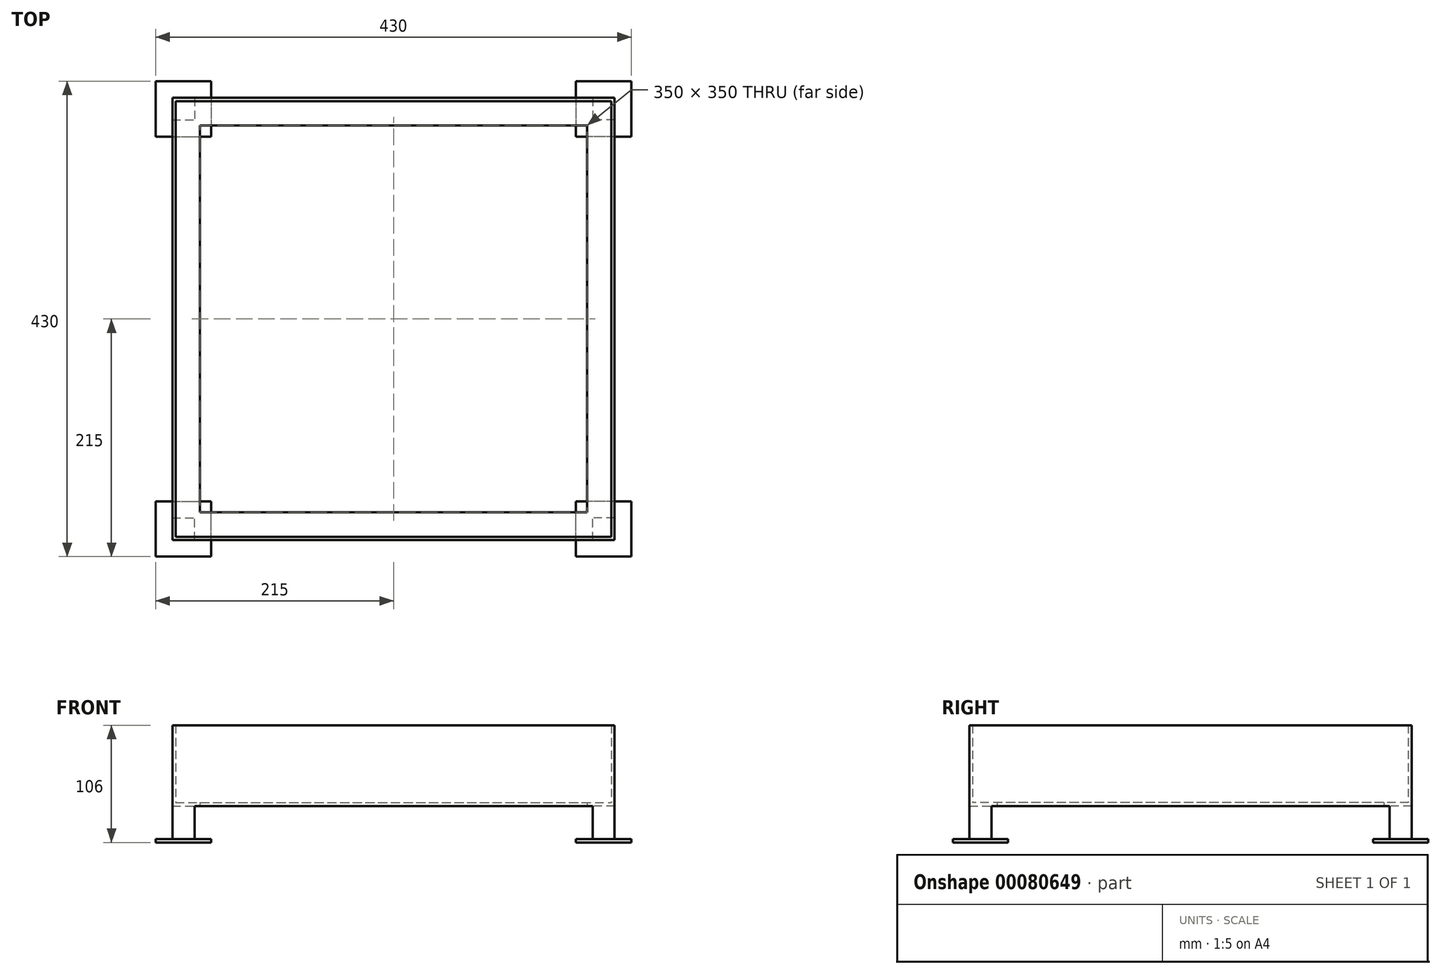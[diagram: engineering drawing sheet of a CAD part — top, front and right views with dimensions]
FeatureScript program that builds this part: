
annotation { "Feature Type Name" : "Feature", "Feature Type Description" : "" }
export const myFeature = defineFeature(function(context is Context, id is Id, definition is map)
    precondition{}
    {
        {
            var Q0;
            Q0=qCreatedBy(makeId("Top.planeOp"),FACE);
            var sketch = newSketch(context, id + "F0", { "sketchPlane" : qUnion([Q0])});
            skLineSegment(sketch, "E0.bottom", {"start": v(-200, 200) * mm, "end": v(200, 200) * mm});
            skLineSegment(sketch, "E0.top", {"start": v(-200, -200) * mm, "end": v(200, -200) * mm});
            skLineSegment(sketch, "E0.left", {"start": v(-200, 200) * mm, "end": v(-200, -200) * mm});
            skLineSegment(sketch, "E0.right", {"start": v(200, 200) * mm, "end": v(200, -200) * mm});
            skPoint(sketch, "E0.middle", {"position": v(0, 0) * mm});
            skLineSegment(sketch, "E1.bottom", {"start": v(-175, 175) * mm, "end": v(175, 175) * mm});
            skLineSegment(sketch, "E1.top", {"start": v(-175, -175) * mm, "end": v(175, -175) * mm});
            skLineSegment(sketch, "E1.left", {"start": v(-175, 175) * mm, "end": v(-175, -175) * mm});
            skLineSegment(sketch, "E1.right", {"start": v(175, 175) * mm, "end": v(175, -175) * mm});
            skSolve(sketch);
        }
        {
            var Q0;
            Q0=makeQuery(id+"F0.imprint","IMPRINT",FACE,{"disambiguationData":[TD([[makeQuery(id+"F0.imprint","IMPRINT",EDGE,{"derivedFrom":sQuery(id+"F0.wireOp",EDGE,"E0.bottom")}),-1.0]])]});
            extrude(context, id + "F1", {"entities" : qUnion([Q0]), "depth" : 3 * mm});
        }
        {
            var Q0;
            Q0=makeQuery(id+"F1.opExtrude","CAP_FACE",FACE,{"disambiguationData":[OSD([sQuery(id+"F0.wireOp",EDGE,"E0.bottom"),sQuery(id+"F0.wireOp",EDGE,"E0.top"),sQuery(id+"F0.wireOp",EDGE,"E0.left"),sQuery(id+"F0.wireOp",EDGE,"E0.right"),sQuery(id+"F0.wireOp",EDGE,"E1.bottom"),sQuery(id+"F0.wireOp",EDGE,"E1.top"),sQuery(id+"F0.wireOp",EDGE,"E1.left"),sQuery(id+"F0.wireOp",EDGE,"E1.right")])],"isStart":false});
            var sketch = newSketch(context, id + "F2", { "sketchPlane" : qUnion([Q0])});
            skLineSegment(sketch, "E2.0", {"start": v(-200, 200) * mm, "end": v(-200, -200) * mm});
            skLineSegment(sketch, "E3.0", {"start": v(-200, 200) * mm, "end": v(200, 200) * mm});
            skLineSegment(sketch, "E4.0", {"start": v(200, 200) * mm, "end": v(200, -200) * mm});
            skLineSegment(sketch, "E5.0", {"start": v(-200, -200) * mm, "end": v(200, -200) * mm});
            skLineSegment(sketch, "E6.bottom", {"start": v(-197, 197) * mm, "end": v(197, 197) * mm});
            skLineSegment(sketch, "E6.top", {"start": v(-197, -197) * mm, "end": v(197, -197) * mm});
            skLineSegment(sketch, "E6.left", {"start": v(-197, 197) * mm, "end": v(-197, -197) * mm});
            skLineSegment(sketch, "E6.right", {"start": v(197, 197) * mm, "end": v(197, -197) * mm});
            skPoint(sketch, "E6.middle", {"position": v(0, 0) * mm});
            skSolve(sketch);
        }
        {
            var Q0;
            Q0=makeQuery(id+"F2.imprint","IMPRINT",FACE,{"disambiguationData":[TD([[makeQuery(id+"F2.imprint","IMPRINT",EDGE,{"derivedFrom":sQuery(id+"F2.wireOp",EDGE,"E2.0")}),1.0]])]});
            extrude(context, id + "F3", {"entities" : qUnion([Q0]), "operationType" : NewBodyOperationType.ADD, "depth" : 70 * mm});
        }
        {
            var Q0;
            Q0=makeQuery(id+"F1.opExtrude","CAP_FACE",FACE,{"disambiguationData":[OSD([sQuery(id+"F0.wireOp",EDGE,"E0.bottom"),sQuery(id+"F0.wireOp",EDGE,"E0.top"),sQuery(id+"F0.wireOp",EDGE,"E0.left"),sQuery(id+"F0.wireOp",EDGE,"E0.right"),sQuery(id+"F0.wireOp",EDGE,"E1.bottom"),sQuery(id+"F0.wireOp",EDGE,"E1.top"),sQuery(id+"F0.wireOp",EDGE,"E1.left"),sQuery(id+"F0.wireOp",EDGE,"E1.right")])],"isStart":true});
            var sketch = newSketch(context, id + "F4", { "sketchPlane" : qUnion([Q0])});
            skLineSegment(sketch, "E7.bottom", {"start": v(-200, 200) * mm, "end": v(-180, 200) * mm});
            skLineSegment(sketch, "E7.top", {"start": v(-200, 180) * mm, "end": v(-180, 180) * mm});
            skLineSegment(sketch, "E7.left", {"start": v(-200, 200) * mm, "end": v(-200, 180) * mm});
            skLineSegment(sketch, "E7.right", {"start": v(-180, 200) * mm, "end": v(-180, 180) * mm});
            skLineSegment(sketch, "E8.MirrorCS", {"start": v(200, 180) * mm, "end": v(180, 180) * mm});
            skLineSegment(sketch, "E9.MirrorCS", {"start": v(200, 200) * mm, "end": v(200, 180) * mm});
            skLineSegment(sketch, "E10.MirrorCS", {"start": v(200, 200) * mm, "end": v(180, 200) * mm});
            skLineSegment(sketch, "E11.MirrorCS", {"start": v(180, 200) * mm, "end": v(180, 180) * mm});
            skLineSegment(sketch, "E12.MirrorCS", {"start": v(-200, -180) * mm, "end": v(-180, -180) * mm});
            skLineSegment(sketch, "E13.MirrorCS", {"start": v(-200, -200) * mm, "end": v(-200, -180) * mm});
            skLineSegment(sketch, "E14.MirrorCS", {"start": v(-200, -200) * mm, "end": v(-180, -200) * mm});
            skLineSegment(sketch, "E15.MirrorCS", {"start": v(-180, -200) * mm, "end": v(-180, -180) * mm});
            skLineSegment(sketch, "E16.MirrorCS", {"start": v(180, -200) * mm, "end": v(180, -180) * mm});
            skLineSegment(sketch, "E17.MirrorCS", {"start": v(200, -200) * mm, "end": v(180, -200) * mm});
            skLineSegment(sketch, "E18.MirrorCS", {"start": v(200, -200) * mm, "end": v(200, -180) * mm});
            skLineSegment(sketch, "E19.MirrorCS", {"start": v(200, -180) * mm, "end": v(180, -180) * mm});
            skSolve(sketch);
        }
        {
            var Q0;
            Q0 = qSketchRegion(id + "F4", true);
            extrude(context, id + "F5", {"entities" : qUnion([Q0]), "operationType" : NewBodyOperationType.ADD, "depth" : 30 * mm});
        }
        {
            var Q0;
            Q0=makeQuery(id+"F5.opExtrude","CAP_FACE",FACE,{"disambiguationData":[OSD([sQuery(id+"F4.wireOp",EDGE,"E7.bottom"),sQuery(id+"F4.wireOp",EDGE,"E7.top"),sQuery(id+"F4.wireOp",EDGE,"E7.left"),sQuery(id+"F4.wireOp",EDGE,"E7.right")])],"isStart":false});
            var sketch = newSketch(context, id + "F6", { "sketchPlane" : qUnion([Q0])});
            skPoint(sketch, "E20", {"position": v(-200, 190) * mm});
            skPoint(sketch, "E21", {"position": v(-180, 190) * mm});
            skLineSegment(sketch, "E22", {"start": v(-200, 190) * mm, "end": v(-180, 190) * mm, "construction": true});
            skPoint(sketch, "E23", {"position": v(-190, 190) * mm});
            skLineSegment(sketch, "E24.bottom", {"start": v(-215, 215) * mm, "end": v(-165, 215) * mm});
            skLineSegment(sketch, "E24.top", {"start": v(-215, 165) * mm, "end": v(-165, 165) * mm});
            skLineSegment(sketch, "E24.left", {"start": v(-215, 215) * mm, "end": v(-215, 165) * mm});
            skLineSegment(sketch, "E24.right", {"start": v(-165, 215) * mm, "end": v(-165, 165) * mm});
            skPoint(sketch, "E25.MirrorP", {"position": v(190, 190) * mm});
            skLineSegment(sketch, "E26.MirrorCS", {"start": v(165, 215) * mm, "end": v(165, 165) * mm});
            skLineSegment(sketch, "E27.MirrorCS", {"start": v(215, 215) * mm, "end": v(215, 165) * mm});
            skLineSegment(sketch, "E28.MirrorCS", {"start": v(215, 165) * mm, "end": v(165, 165) * mm});
            skLineSegment(sketch, "E29.MirrorCS", {"start": v(215, 215) * mm, "end": v(165, 215) * mm});
            skLineSegment(sketch, "E30.MirrorCS", {"start": v(200, 190) * mm, "end": v(180, 190) * mm, "construction": true});
            skPoint(sketch, "E31.MirrorP", {"position": v(180, 190) * mm});
            skPoint(sketch, "E32.MirrorP", {"position": v(200, 190) * mm});
            skLineSegment(sketch, "E33.MirrorCS", {"start": v(-200, -190) * mm, "end": v(-180, -190) * mm, "construction": true});
            skLineSegment(sketch, "E34.MirrorCS", {"start": v(200, -190) * mm, "end": v(180, -190) * mm, "construction": true});
            skPoint(sketch, "E35.MirrorP", {"position": v(-190, -190) * mm});
            skPoint(sketch, "E36.MirrorP", {"position": v(190, -190) * mm});
            skLineSegment(sketch, "E37.MirrorCS", {"start": v(215, -215) * mm, "end": v(165, -215) * mm});
            skPoint(sketch, "E38.MirrorP", {"position": v(200, -190) * mm});
            skPoint(sketch, "E39.MirrorP", {"position": v(180, -190) * mm});
            skPoint(sketch, "E40.MirrorP", {"position": v(-180, -190) * mm});
            skLineSegment(sketch, "E41.MirrorCS", {"start": v(215, -215) * mm, "end": v(215, -165) * mm});
            skLineSegment(sketch, "E42.MirrorCS", {"start": v(-215, -215) * mm, "end": v(-165, -215) * mm});
            skPoint(sketch, "E43.MirrorP", {"position": v(-200, -190) * mm});
            skLineSegment(sketch, "E44.MirrorCS", {"start": v(165, -215) * mm, "end": v(165, -165) * mm});
            skLineSegment(sketch, "E45.MirrorCS", {"start": v(-165, -215) * mm, "end": v(-165, -165) * mm});
            skLineSegment(sketch, "E46.MirrorCS", {"start": v(-215, -215) * mm, "end": v(-215, -165) * mm});
            skLineSegment(sketch, "E47.MirrorCS", {"start": v(215, -165) * mm, "end": v(165, -165) * mm});
            skLineSegment(sketch, "E48.MirrorCS", {"start": v(-215, -165) * mm, "end": v(-165, -165) * mm});
            skSolve(sketch);
        }
        {
            var Q0;
            Q0 = qSketchRegion(id + "F6", true);
            extrude(context, id + "F7", {"entities" : qUnion([Q0]), "operationType" : NewBodyOperationType.ADD, "depth" : 3 * mm});
        }
    });
